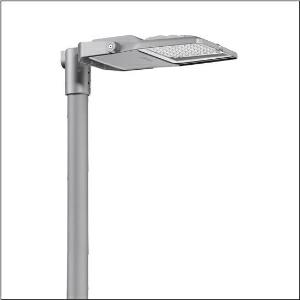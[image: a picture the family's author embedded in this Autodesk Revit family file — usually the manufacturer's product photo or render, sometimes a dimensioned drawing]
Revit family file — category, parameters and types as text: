
# Revit family: floodlight_fl_21_mini___pl43_5xa7776c2a3a_c8bd
name_source: partatom
category: Lighting Fixtures
units: mm (PartAtom-declared; Revit-internal decimal feet)

## family parameters
Cut with Voids When Loaded = No
Host = Face
Light Source = No
Part Type = Normal
Room Calculation Point = No
Round Connector Dimension = Use Diameter
Shared = No

## types (1)
- --- (1 x LED, 12500 lm, 89 W, 3000K)
    Apparent Load = 89 VA
    CIE Flux Codes = 27 78 99 100 100
    Color Rendering = 70
    Color Temperature = 3000K
    Default Elevation = 1800 mm
    Description = Floodlight FL 21 mini, floodlight, primary light control with lens, of PMMA, primary optical cover: protective disc, of toughened safety glass, transparent, light distribution: PL43, light emission: direct distribution, installation type: surface-mounted, LED, High Power LED, rated luminous flux: 12.500lm, luminous efficacy: 140lm/W, light colour: 730, colour temperature: 3000K, control: flexible luminous flux parameterisation, time-dependent luminous flux control, constant luminous flux control, overheat protection, pre-setting: logarithmic dimming characteristic, with terminal, 6-pole, mains connection: 220..240V, AC, 50/60Hz, start of lifetime: 89W, end of service life: 94W, reduction: 43W, luminaire housing, of diecast aluminium, powder-coated, Siteco® metallic grey (DB 702S), corrosivity category C5 mid according to DIN EN ISO 12944, sealing non-destructively replaceable, please order mast flange separately, mast bracket, of steel, galvanised, powder-coated, Siteco® metallic grey (DB 702S), Smart Interface below and above, protection rating (complete): IP66, insulation class (complete): insulation class II (safety insulation), certification: CE, ENEC, VDE, protection symbol: D, impact resistance: IK08, permissible operating ambient temperature: -40..+40°C, permissible operating ambient temperature for outdoor applications: -40..+50°C, standard: DIN EN 12944, LABS conformity tested according to VDMA 24364:2018-05, packaging unit: 1 piece

Light Distribution: PL43
    Height = 70 mm
    Lamp = 1 x LED
    Lamp Light Flux = 12500 lm
    Lamp Power = 89 W
    Lamp count = 1
    Length = 485 mm
    Luminous efficacy = 140 lm/W
    Manufacturer = Siteco
    ModVariant = No
    Model = 5XA7776C2A3A
    Number of Poles = 1
    OnlyDefault = Yes
    Power Factor = 1
    Product Name = Floodlight FL 21 mini | PL43
    Product group = floodlight | pylon annexe
    ProductGroupID = 6200
    Protection Class = Protection class II
    Protection Degree = IP 66
    RLX_Detail_Level = 1
    RLX_Emergency_Light_Flux = 0 lm
    RLX_Emergency_Type = 0
    RLX_Emergency_Type_DB = No
    RlxData = <blob elided: 100825 chars, md5=294408c1>
    Socket = socket
    Standby Power = 0 W
    System Light Flux = 12500 lm
    System Power = 89 W
    Type Comments = factory setting: luminous flux: 100 % | dim-lin: 254 | 456 mA
    Type Image = l_1007125.jpg
    URL = http://relux.com
    VarID = @adj_131429
    Voltage = 0 V
    Weight = 0.00 kg
    Width = 337 mm

## geometry (parser evidence)
native form markers: Blend x4, Sweep x13
no freeform markers — native parametric forms only
